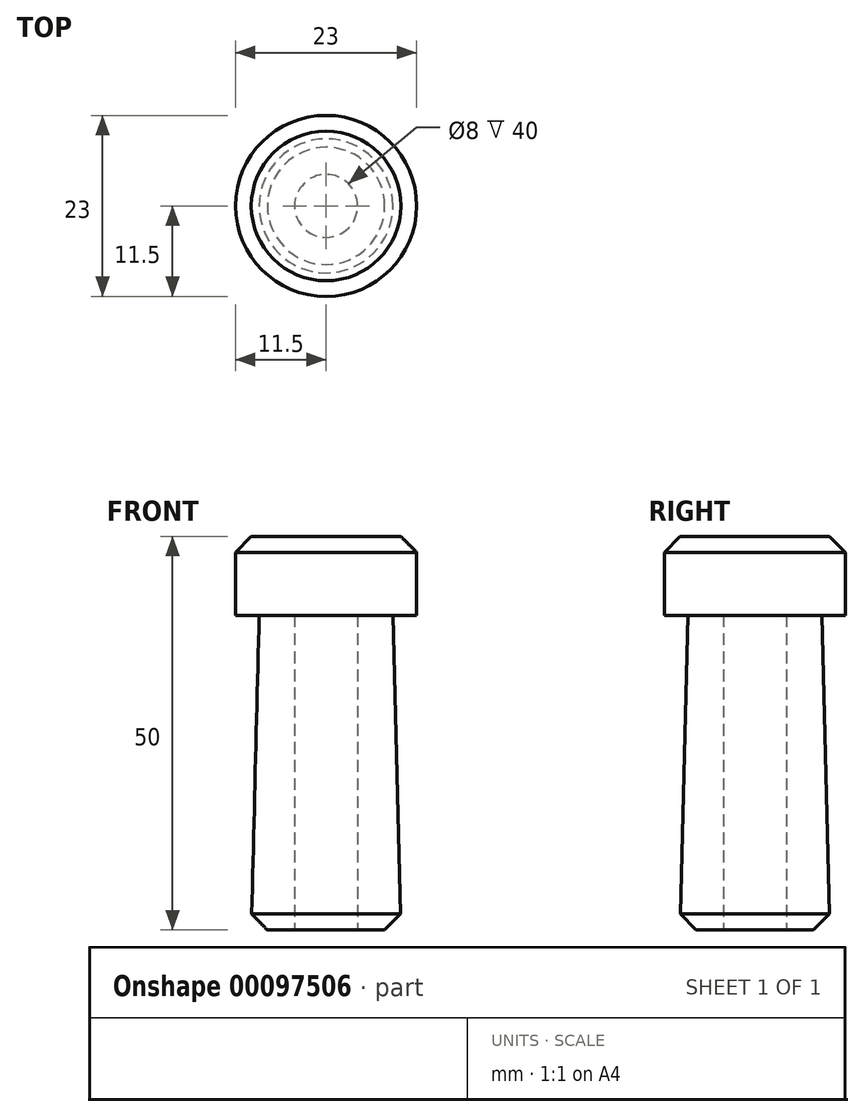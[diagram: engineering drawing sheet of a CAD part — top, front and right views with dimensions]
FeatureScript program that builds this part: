
annotation { "Feature Type Name" : "Feature", "Feature Type Description" : "" }
export const myFeature = defineFeature(function(context is Context, id is Id, definition is map)
    precondition{}
    {
        {
            var Q0;
            Q0=qCreatedBy(makeId("Front.planeOp"),FACE);
            var sketch = newSketch(context, id + "F0", { "sketchPlane" : qUnion([Q0])});
            skLineSegment(sketch, "E0", {"start": v(0, 0) * mm, "end": v(9.5, 0) * mm});
            skLineSegment(sketch, "E1", {"start": v(9.5, 0) * mm, "end": v(8.5, 40) * mm});
            skLineSegment(sketch, "E2", {"start": v(0, 0) * mm, "end": v(0, 40) * mm});
            skLineSegment(sketch, "E3", {"start": v(0, 40) * mm, "end": v(0, 50) * mm});
            skLineSegment(sketch, "E4", {"start": v(0, 50) * mm, "end": v(8.5, 50) * mm});
            skLineSegment(sketch, "E5", {"start": v(8.5, 40) * mm, "end": v(11.5, 40) * mm});
            skLineSegment(sketch, "E6", {"start": v(11.5, 40) * mm, "end": v(11.5, 50) * mm});
            skLineSegment(sketch, "E7", {"start": v(11.5, 50) * mm, "end": v(8.5, 50) * mm});
            skSolve(sketch);
        }
        {
            var Q0;
            Q0=makeQuery(id+"F0.imprint","IMPRINT",FACE,{"disambiguationData":[TD([[makeQuery(id+"F0.imprint","IMPRINT",EDGE,{"derivedFrom":sQuery(id+"F0.wireOp",EDGE,"E0")}),1.0]])]});
            var Q1;
            Q1=sQuery(id+"F0.wireOp",EDGE,"E3");
            revolve(context, id + "F1", {"entities" : qUnion([Q0]), "axis" : qUnion([Q1]), "revolveType" : RevolveType.FULL});
        }
        {
            var Q0;
            Q0=makeQuery(id+"F1.opRevolve","SWEPT_EDGE",EDGE,{"disambiguationData":[OSD([sQuery(id+"F0.wireOp",EDGE,"E0"),sQuery(id+"F0.wireOp",EDGE,"E1")])]});
            chamfer(context, id + "F2", {"entities" : qUnion([Q0]), "width" : 2 * mm, "tangentPropagation" : true});
        }
        {
            var Q0;
            Q0=makeQuery(id+"F1.opRevolve","SWEPT_EDGE",EDGE,{"disambiguationData":[OSD([sQuery(id+"F0.wireOp",EDGE,"E6"),sQuery(id+"F0.wireOp",EDGE,"E7")])]});
            chamfer(context, id + "F3", {"entities" : qUnion([Q0]), "width" : 2 * mm, "tangentPropagation" : true});
        }
        {
            var Q0;
            Q0=makeQuery(id+"F1.opRevolve","SWEPT_FACE",FACE,{"disambiguationData":[OSD([sQuery(id+"F0.wireOp",EDGE,"E0")])]});
            var sketch = newSketch(context, id + "F4", { "sketchPlane" : qUnion([Q0])});
            skCircle(sketch, "E8", {"center": v(0, 0) * mm, "radius": 4 * mm});
            skSolve(sketch);
        }
        {
            var Q0;
            Q0=makeQuery(id+"F4.imprint","IMPRINT",FACE,{"disambiguationData":[TD([[makeQuery(id+"F4.imprint","IMPRINT",EDGE,{"derivedFrom":sQuery(id+"F4.wireOp",EDGE,"E8")}),1.0]])]});
            var Q1;
            Q1=makeQuery(id+"F1.opRevolve","SWEPT_FACE",FACE,{"disambiguationData":[OSD([sQuery(id+"F0.wireOp",EDGE,"E5")])]});
            extrude(context, id + "F5", {"entities" : qUnion([Q0]), "operationType" : NewBodyOperationType.REMOVE, "endBound" : BoundingType.UP_TO_SURFACE, "oppositeDirection" : true, "endBoundEntityFace" : qUnion([Q1]), "depth" : 25 * mm});
        }
    });
